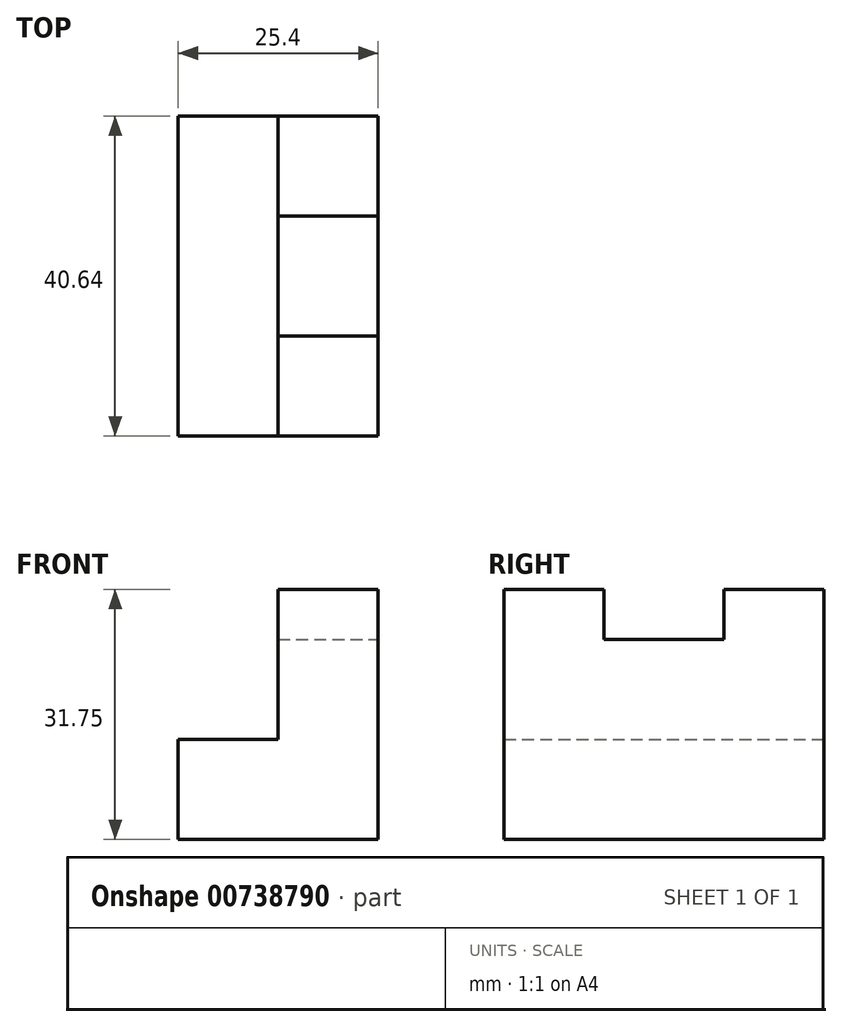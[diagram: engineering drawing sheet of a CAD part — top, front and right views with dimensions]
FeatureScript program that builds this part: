
annotation { "Feature Type Name" : "Feature", "Feature Type Description" : "" }
export const myFeature = defineFeature(function(context is Context, id is Id, definition is map)
    precondition{}
    {
        {
            var Q0;
            Q0=qCreatedBy(makeId("Front.planeOp"),FACE);
            var sketch = newSketch(context, id + "F0", { "sketchPlane" : qUnion([Q0])});
            skLineSegment(sketch, "E0", {"start": v(0, 31.75) * mm, "end": v(0, 0) * mm});
            skLineSegment(sketch, "E1", {"start": v(0, 0) * mm, "end": v(-25.4, 0) * mm});
            skLineSegment(sketch, "E2", {"start": v(-25.4, 0) * mm, "end": v(-25.4, 12.7) * mm});
            skLineSegment(sketch, "E3", {"start": v(-25.4, 12.7) * mm, "end": v(-12.7, 12.7) * mm});
            skLineSegment(sketch, "E4", {"start": v(-12.7, 12.7) * mm, "end": v(-12.7, 31.75) * mm});
            skLineSegment(sketch, "E5", {"start": v(-12.7, 31.75) * mm, "end": v(0, 31.75) * mm});
            skSolve(sketch);
        }
        {
            var Q0;
            Q0 = qSketchRegion(id + "F0", true);
            extrude(context, id + "F1", {"entities" : qUnion([Q0]), "depth" : 40.64 * mm, "offsetDistance" : 25.4 * mm});
        }
        {
            var Q0;
            Q0=qCreatedBy(makeId("Right.planeOp"),FACE);
            var sketch = newSketch(context, id + "F2", { "sketchPlane" : qUnion([Q0])});
            skLineSegment(sketch, "E6", {"start": v(-12.7, 31.75) * mm, "end": v(-12.7, 25.4) * mm});
            skLineSegment(sketch, "E7", {"start": v(-12.7, 25.4) * mm, "end": v(-27.94, 25.4) * mm});
            skLineSegment(sketch, "E8", {"start": v(-27.94, 25.4) * mm, "end": v(-27.94, 31.75) * mm});
            skLineSegment(sketch, "E9", {"start": v(-27.94, 31.75) * mm, "end": v(-12.7, 31.75) * mm});
            skSolve(sketch);
        }
        {
            var Q0;
            Q0 = qSketchRegion(id + "F2", true);
            extrude(context, id + "F3", {"entities" : qUnion([Q0]), "operationType" : NewBodyOperationType.REMOVE, "oppositeDirection" : true, "depth" : 12.7 * mm, "offsetDistance" : 25.4 * mm});
        }
    });
